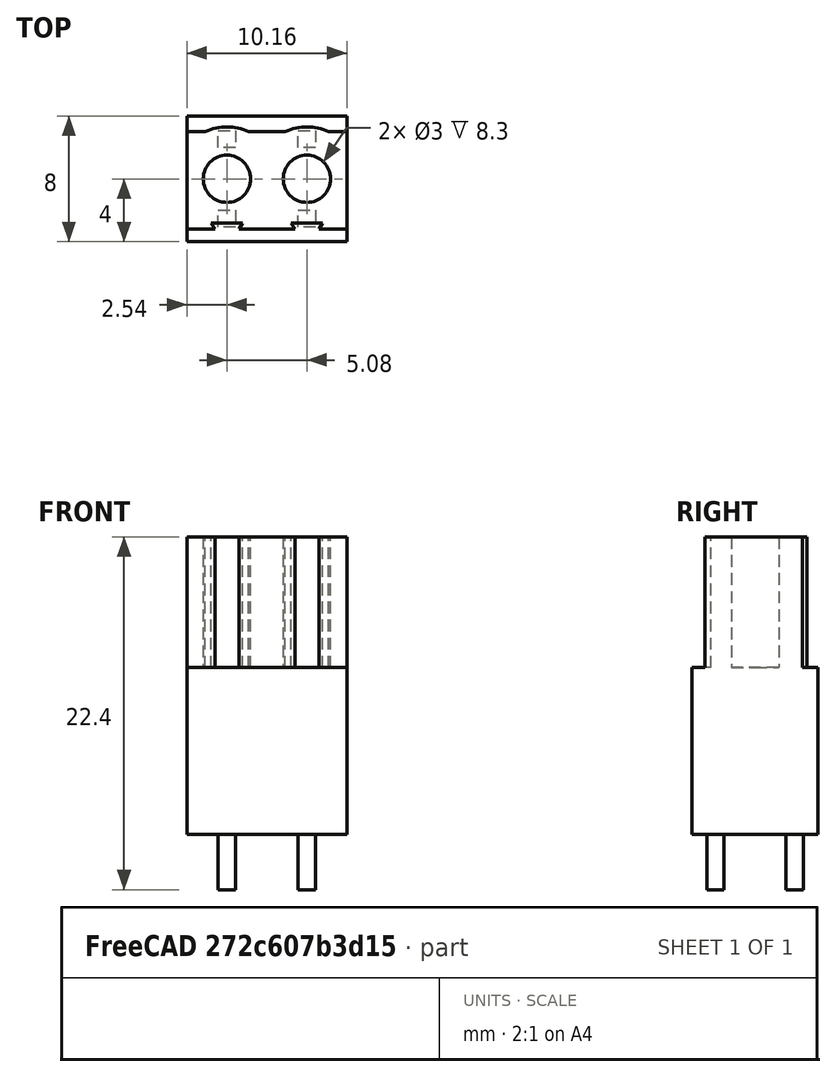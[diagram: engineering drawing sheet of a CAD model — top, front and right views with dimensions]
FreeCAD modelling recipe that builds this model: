
FCSTD DOCUMENT  (FreeCAD 1.1R44227 +647 (Git))
Label: 950066002000000
License: All rights reserved
objects: Sketcher::SketchObject×3, PartDesign::Pad×3, App::Point×1, PartDesign::Body×1, PartDesign::LinearPattern×1
note: 18 computed .brp shape members not serialized (recipe doc carries the construction recipe); baked Part::Feature solids carry a one-line shape summary decoded from their .brp

FEATURE [App::Point] Origin001
  Role = Origin
FEATURE [Sketcher::SketchObject] Sketch
  ArcFitTolerance = 1e-06
  AttachmentSupport = -> [Origin]
  ExternalTypes = [0]
  FullyConstrained = true
  MakeInternals = false
  MapMode = 5
  _ExternalGeoVersion = 1
  sketch-geometry (4):
    g0: LineSegment StartX=-2.54 StartY=4 StartZ=0 EndX=-2.54 EndY=-4 EndZ=0
    g1: LineSegment StartX=-2.54 StartY=-4 StartZ=0 EndX=7.62 EndY=-4 EndZ=0
    g2: LineSegment StartX=7.62 StartY=-4 StartZ=0 EndX=7.62 EndY=4 EndZ=0
    g3: LineSegment StartX=7.62 StartY=4 StartZ=0 EndX=-2.54 EndY=4 EndZ=0
  constraints (12):
    c: Coincident(g0,g1)
    c: Coincident(g1,g2)
    c: Coincident(g2,g3)
    c: Coincident(g3,g0)
    c: Vertical(g0)
    c: Vertical(g2)
    c: Horizontal(g1)
    c: Horizontal(g3)
    c: Distance(g0,g0) = 8
    c: DistanceY(g-1,g0) = 4
    c: DistanceX(g3,g3) = 10.16
    c: DistanceX(g0,g-1) = 2.54
FEATURE [PartDesign::Pad] Pad
  Direction = (0,0,1)
  Length = 10.6
  Length2 = 10
  Profile = -> Sketch
  ReferenceAxis = -> Sketch [N_Axis]
  Refine = true
  SideType = 0
  Suppressed = false
  Type = 0
  Type2 = 0
FEATURE [Sketcher::SketchObject] Sketch001
  ArcFitTolerance = 1e-06
  AttachmentSupport = -> [Pad]
  ExternalTypes = [0]
  FullyConstrained = true
  MakeInternals = false
  MapMode = 5
  Placement = pos=(0,0,10.6) rot=(0,0,1;0rad)
  _ExternalGeoVersion = 1
  sketch-geometry (18):
    g0: Circle CenterX=0 CenterY=0 CenterZ=0 NormalX=0 NormalY=0 NormalZ=1 AngleXU=0 Radius=1.5
    g1: ArcOfCircle CenterX=0 CenterY=0 CenterZ=0 NormalX=0 NormalY=0 NormalZ=1 AngleXU=0 Radius=3.3 StartAngle=1.1411 EndAngle=2.0005
    g2: LineSegment StartX=-1.37477 StartY=3 StartZ=0 EndX=-2.54 EndY=3 EndZ=0
    g3: LineSegment StartX=1.37477 StartY=3 StartZ=0 EndX=2.54 EndY=3 EndZ=0
    g4: LineSegment [constr] StartX=-1.37477 StartY=3 StartZ=0 EndX=1.37477 EndY=3 EndZ=0
    g5: LineSegment StartX=2.54 StartY=3 StartZ=0 EndX=2.54 EndY=-3.2 EndZ=0
    g6: LineSegment StartX=2.54 StartY=-3.2 StartZ=0 EndX=0.76906 EndY=-3.2 EndZ=0
    g7: LineSegment StartX=-2.54 StartY=-3.2 StartZ=0 EndX=-2.54 EndY=3 EndZ=0
    g8: LineSegment [constr] StartX=0 StartY=0 StartZ=0 EndX=2.54 EndY=3 EndZ=0
    g9: LineSegment [constr] StartX=0 StartY=0 StartZ=0 EndX=-2.54 EndY=3 EndZ=0
    g10: LineSegment StartX=-0.76906 StartY=-3.2 StartZ=0 EndX=-2.54 EndY=-3.2 EndZ=0
    g11: LineSegment StartX=-0.76906 StartY=-3.2 StartZ=0 EndX=-1 EndY=-2.8 EndZ=0
    g12: LineSegment StartX=-1 StartY=-2.8 StartZ=0 EndX=1 EndY=-2.8 EndZ=0
    g13: LineSegment StartX=1 StartY=-2.8 StartZ=0 EndX=0.76906 EndY=-3.2 EndZ=0
    g14: LineSegment [constr] StartX=-0.76906 StartY=-3.2 StartZ=0 EndX=0.76906 EndY=-3.2 EndZ=0
    g15: LineSegment [constr] StartX=-0.76906 StartY=-3.2 StartZ=0 EndX=1 EndY=-2.8 EndZ=0
    g16: LineSegment [constr] StartX=-1 StartY=-2.8 StartZ=0 EndX=0.76906 EndY=-3.2 EndZ=0
    g17: GeomPoint [constr] X=0 Y=-3.2 Z=0
  constraints (45):
    c: Coincident(g0,g-1)
    c: Diameter(g0) = 3
    c: Coincident(g1,g0)
    c: Coincident(g2,g1)
    c: Horizontal(g2)
    c: Coincident(g3,g1)
    c: Horizontal(g3)
    c: Coincident(g4,g1)
    c: Coincident(g4,g1)
    c: Horizontal(g4)
    c: Coincident(g5,g3)
    c: Vertical(g5)
    c: Coincident(g6,g5)
    c: Coincident(g7,g10)
    c: Coincident(g7,g2)
    c: Vertical(g7)
    c: Coincident(g8,g0)
    c: Coincident(g8,g3)
    c: Coincident(g9,g0)
    c: Coincident(g9,g2)
    c: Equal(g9,g8)
    c: Distance(g6,g10) = 5.08
    c: Radius(g1) = 3.3
    c: DistanceY(g-1,g2) = 3
    c: DistanceY(g7,g7) = 6.2
    c: Horizontal(g6)
    c: Horizontal(g10)
    c: Coincident(g11,g10)
    c: Coincident(g12,g11)
    c: Horizontal(g12)
    c: Coincident(g13,g12)
    c: Coincident(g13,g6)
    c: Coincident(g14,g10)
    c: Coincident(g14,g6)
    c: Horizontal(g14)
    c: Coincident(g15,g10)
    c: Coincident(g15,g12)
    c: Coincident(g16,g11)
    c: Coincident(g16,g6)
    c: Equal(g15,g16)
    c: Angle(g11,g10) = 1.0472
    c: DistanceX(g12,g12) = 2
    c: DistanceY(g6,g12) = 0.4
    c: Symmetric(g14,g14,g17)
    c: PointOnObject(g17,g-2)
FEATURE [PartDesign::Pad] Pad001
  BaseFeature = -> Pad
  Direction = (0,0,1)
  Length = 8.3
  Length2 = 10
  Profile = -> Sketch001
  ReferenceAxis = -> Sketch001 [N_Axis]
  Refine = true
  SideType = 0
  Suppressed = false
  Type = 0
  Type2 = 0
FEATURE [PartDesign::Body] Body
  AllowCompound = false
  Group = -> [Sketch,Pad,Sketch001,Pad001,LinearPattern,Sketch002,Pad002]
  Origin = -> Origin
  Tip = -> Pad002
FEATURE [PartDesign::LinearPattern] LinearPattern
  BaseFeature = -> Pad001
  Direction = -> Sketch001 [H_Axis]
  Direction2 = -> Sketch001 [V_Axis]
  Length = 5.08
  Length2 = 100
  Mode = 0
  Mode2 = 0
  Occurrences = 2
  Occurrences2 = 1
  Offset = 5.08
  Offset2 = 100
  Originals = -> [Pad001,Pad002]
  Refine = true
  Reversed2 = false
  SpacingPattern = [0]
  SpacingPattern2 = [0]
  Spacings = [-1]
  Suppressed = false
  TransformMode = 0
FEATURE [Sketcher::SketchObject] Sketch002
  ArcFitTolerance = 1e-06
  AttachmentSupport = -> [LinearPattern]
  ExternalGeometry = -> [LinearPattern]
  ExternalTypes = [0]
  FullyConstrained = true
  MakeInternals = false
  MapMode = 5
  Placement = pos=(0,0,0) rot=(1,0,0;3.14159rad)
  _ExternalGeoVersion = 1
  sketch-geometry (10):
    g0: LineSegment StartX=-0.55 StartY=3.07 StartZ=0 EndX=-0.55 EndY=1.97 EndZ=0
    g1: LineSegment StartX=-0.55 StartY=1.97 StartZ=0 EndX=0.55 EndY=1.97 EndZ=0
    g2: LineSegment StartX=0.55 StartY=1.97 StartZ=0 EndX=0.55 EndY=3.07 EndZ=0
    g3: LineSegment StartX=0.55 StartY=3.07 StartZ=0 EndX=-0.55 EndY=3.07 EndZ=0
    g4: GeomPoint [constr] X=0 Y=2.52 Z=0
    g5: LineSegment StartX=-0.55 StartY=-1.97 StartZ=0 EndX=-0.55 EndY=-3.07 EndZ=0
    g6: LineSegment StartX=-0.55 StartY=-3.07 StartZ=0 EndX=0.55 EndY=-3.07 EndZ=0
    g7: LineSegment StartX=0.55 StartY=-3.07 StartZ=0 EndX=0.55 EndY=-1.97 EndZ=0
    g8: LineSegment StartX=0.55 StartY=-1.97 StartZ=0 EndX=-0.55 EndY=-1.97 EndZ=0
    g9: GeomPoint [constr] X=0 Y=-2.52 Z=0
  constraints (26):
    c: Coincident(g0,g1)
    c: Coincident(g1,g2)
    c: Coincident(g2,g3)
    c: Coincident(g3,g0)
    c: Vertical(g0)
    c: Vertical(g2)
    c: Horizontal(g1)
    c: Horizontal(g3)
    c: Symmetric(g2,g0,g4)
    c: PointOnObject(g4,g-2)
    c: Coincident(g5,g6)
    c: Coincident(g6,g7)
    c: Coincident(g7,g8)
    c: Coincident(g8,g5)
    c: Vertical(g5)
    c: Vertical(g7)
    c: Horizontal(g6)
    c: Horizontal(g8)
    c: Symmetric(g7,g5,g9)
    c: PointOnObject(g9,g-2)
    c: Equal(g2,g3)
    c: Equal(g3,g8)
    c: Equal(g8,g7)
    c: Distance(g7,g7) = 1.1
    c: DistanceY(g9,g4) = 5.04
    c: DistanceY(g-6,g9) = 1.48
FEATURE [PartDesign::Pad] Pad002
  BaseFeature = -> LinearPattern
  Direction = (0,0,-1)
  Length = 3.5
  Length2 = 10
  Profile = -> Sketch002
  ReferenceAxis = -> Sketch002 [N_Axis]
  Refine = true
  SideType = 0
  Suppressed = false
  Type = 0
  Type2 = 0
